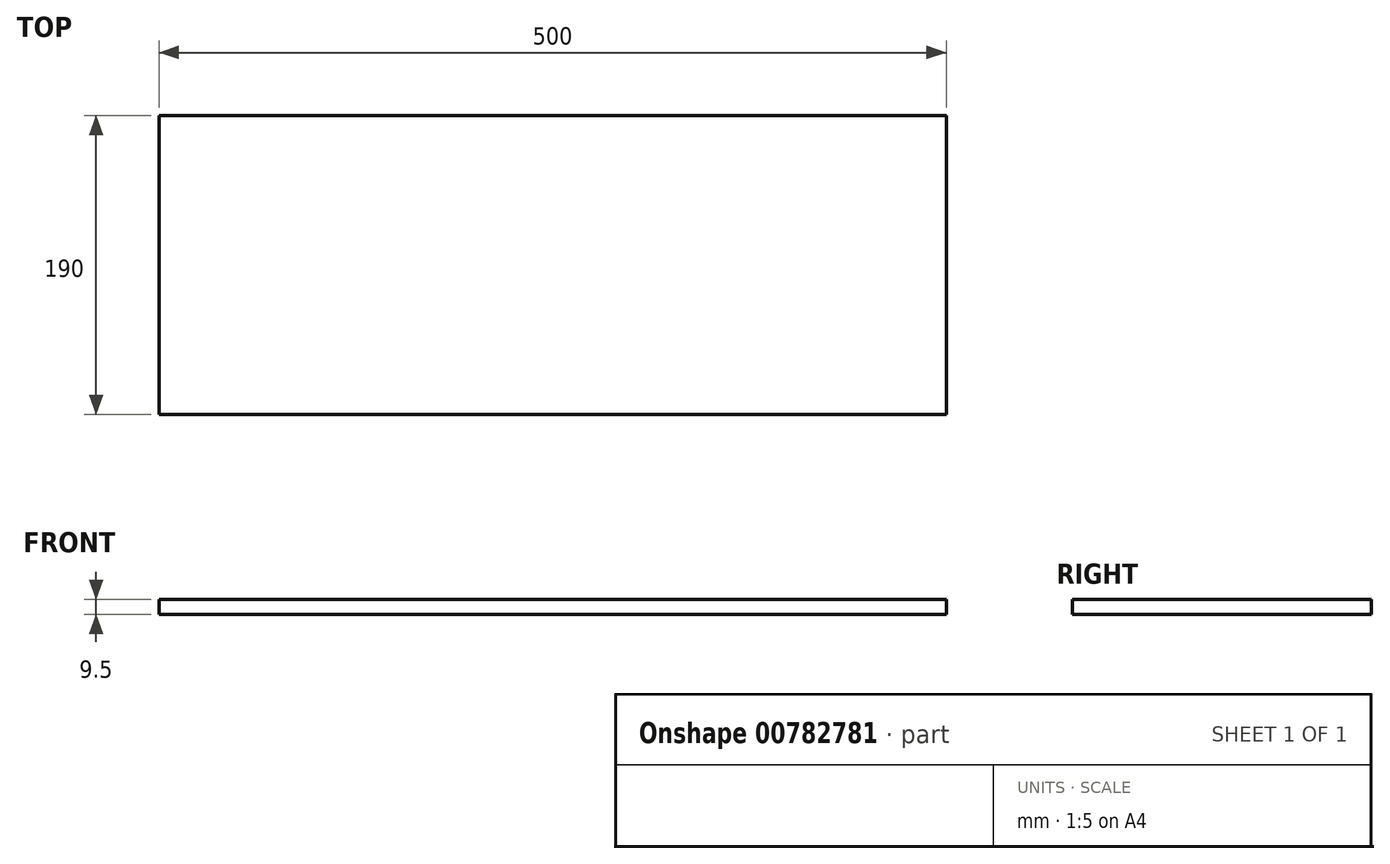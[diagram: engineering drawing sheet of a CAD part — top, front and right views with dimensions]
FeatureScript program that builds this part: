
annotation { "Feature Type Name" : "Feature", "Feature Type Description" : "" }
export const myFeature = defineFeature(function(context is Context, id is Id, definition is map)
    precondition{}
    {
        {
            var Q0;
            Q0=qCreatedBy(makeId("Top.planeOp"),FACE);
            var sketch = newSketch(context, id + "F0", { "sketchPlane" : qUnion([Q0])});
            skLineSegment(sketch, "E0", {"start": v(-31.42, -27.13) * mm, "end": v(468.58, -27.13) * mm});
            skLineSegment(sketch, "E1", {"start": v(468.58, -27.13) * mm, "end": v(468.58, 162.87) * mm});
            skLineSegment(sketch, "E2", {"start": v(-31.42, -27.13) * mm, "end": v(-31.42, 162.87) * mm});
            skLineSegment(sketch, "E3", {"start": v(-31.42, 162.87) * mm, "end": v(468.58, 162.87) * mm});
            skSolve(sketch);
        }
        {
            var Q0;
            Q0=makeQuery(id+"F0.imprint","IMPRINT",FACE,{"disambiguationData":[TD([[makeQuery(id+"F0.imprint","IMPRINT",EDGE,{"derivedFrom":sQuery(id+"F0.wireOp",EDGE,"E0")}),1.0]])]});
            extrude(context, id + "F1", {"entities" : qUnion([Q0]), "depth" : 9.5 * mm, "offsetDistance" : 25 * mm});
        }
    });
